# Revit family: Toilet_Seat-Round_Closed_Front-KOHLER-Span-K-29170IN
name_source: partatom
category: Specialty Equipment
units: mm (PartAtom-declared; Revit-internal decimal feet)

## family parameters
Cut with Voids When Loaded = No
Host = Face
OmniClass Number = 23.31.19.19.17
OmniClass Title = Water Closet Seats
Part Type = Normal
Room Calculation Point = No
Round Connector Dimension = Use Diameter
Shared = No

## types (1)
- 0-White
    ADA Compliant = No
    Assembly Code = C1030200
    Date Modified = 12/14/2022
    Default Elevation = 15"
    Description = Round Quiet Close Toilet Seat
    Finish = Kohler-Plastic-0-White
    Height = 2 3/16"
    Length = 17 15/16"
    Manufacturer = Kohler Co.
    Master Format 2014 = 10 28 00
    Master Format 2014 Name = Toilet, Bath, and Laundry Accessories
    Material = Plastic
    Model = K-29170IN-0
    Product Name = Span
    Product Page URL = https://www.kohler.co.in
    Type = 1
    URL = https://www.kohler.co.in
    WaterSense Certified = No
    Width = 14 11/16"

## geometry (parser evidence)
native form markers: Sweep x5
no freeform markers — native parametric forms only
